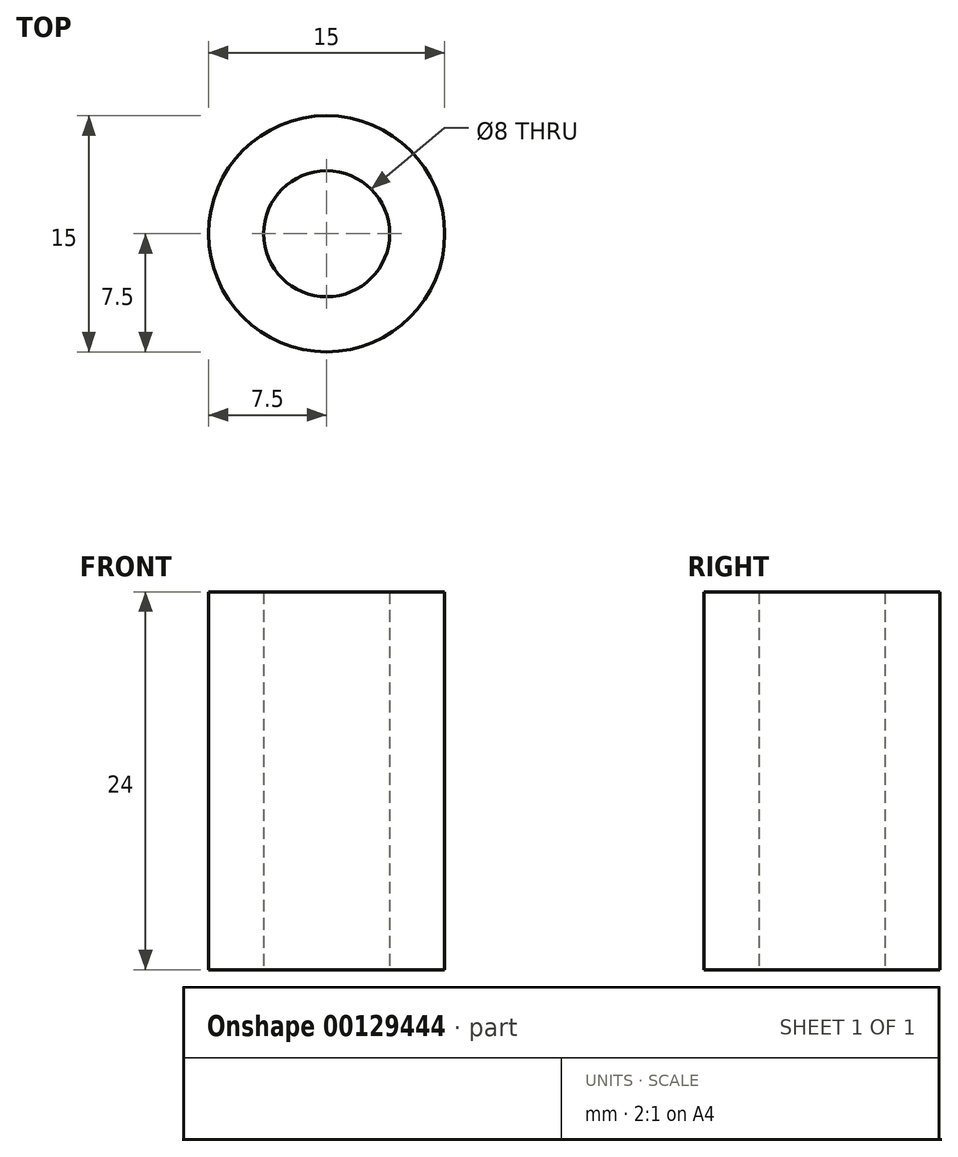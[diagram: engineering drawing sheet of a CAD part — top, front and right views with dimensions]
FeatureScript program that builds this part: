
annotation { "Feature Type Name" : "Feature", "Feature Type Description" : "" }
export const myFeature = defineFeature(function(context is Context, id is Id, definition is map)
    precondition{}
    {
        {
            var Q0;
            Q0=qCreatedBy(makeId("Top.planeOp"),FACE);
            var sketch = newSketch(context, id + "F0", { "sketchPlane" : qUnion([Q0])});
            skCircle(sketch, "E0", {"center": v(0, 0) * mm, "radius": 7.5 * mm});
            skCircle(sketch, "E1", {"center": v(0, 0) * mm, "radius": 4 * mm});
            skSolve(sketch);
        }
        {
            var Q0;
            Q0=qSketchRegion(id+"F0",true);
            extrude(context, id + "F1", {"entities" : qUnion([Q0]), "depth" : 24 * mm});
        }
    });
